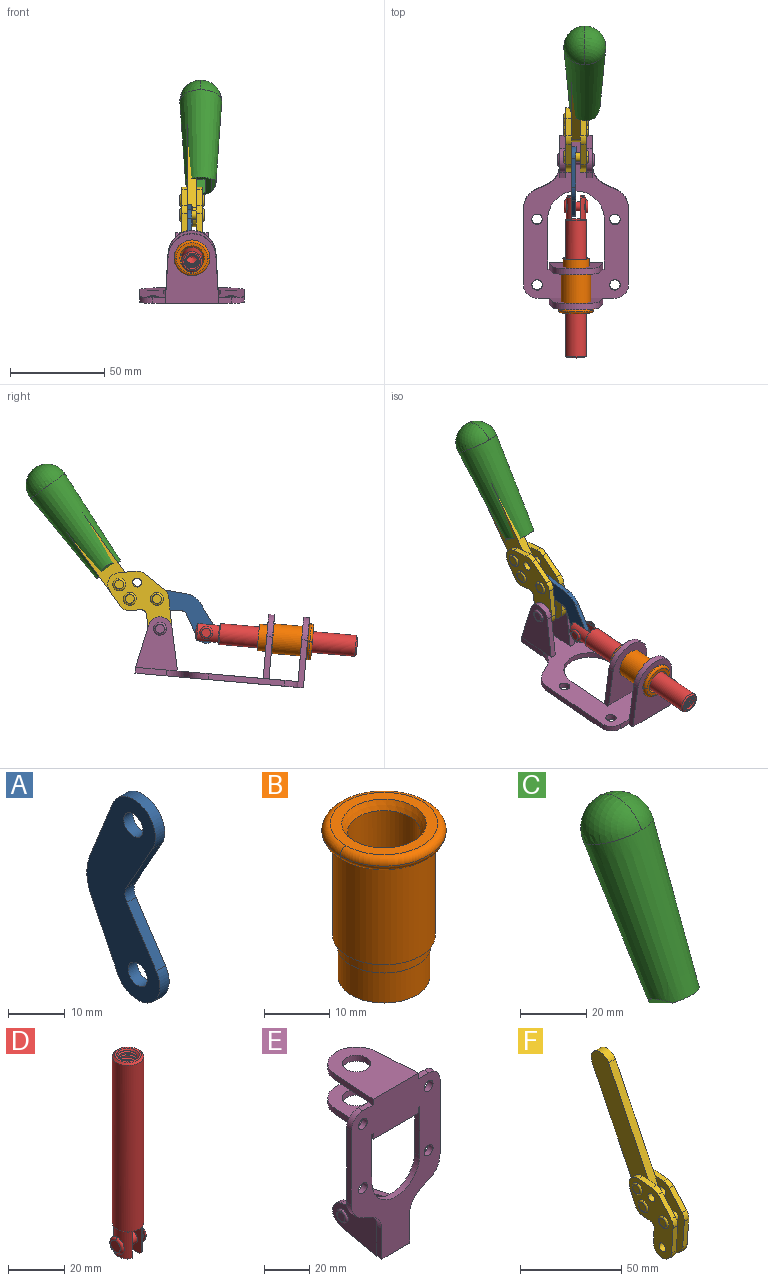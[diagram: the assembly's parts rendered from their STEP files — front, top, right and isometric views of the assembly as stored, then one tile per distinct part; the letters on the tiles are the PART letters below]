
ASSEMBLY  parts=6 mates=6
PART A: 12 faces, bbox 2.3x18.2x42.8 mm
  f0: cylinder r=2.4mm len=4.8mm, axis (1,0,0), area 34.9mm2, adj f4,f11
  f1: cylinder r=10.41mm len=8.47mm, axis (1,0,0), area 20.2mm2, adj f4,f9,f10,f11
  f2: cylinder r=3.05mm len=3.16mm, axis (1,0,0), area 7.7mm2, adj f4,f6,f7,f11
  f3: cylinder r=2.4mm len=4.8mm, axis (1,0,0), area 34.9mm2, adj f4,f11
  f4: plane 42.81x18.23mm, normal (-1,0,0), area 414.1mm2, adj f0,f1,f2,f3,f5,f6,f7,f8
  f5: cylinder r=5.54mm len=10.67mm, axis (1,0,0), area 41.8mm2, adj f4,f6,f10,f11
  f6: plane 11.66x6.53mm, normal (0,-0.87,-0.49), area 30.9mm2, adj f2,f4,f5,f11
  f7: plane 11.17x7.33mm, normal (0,-0.84,0.55), area 30.9mm2, adj f2,f4,f8,f11
  f8: cylinder r=5.54mm len=10.51mm, axis (1,0,0), area 41.8mm2, adj f4,f7,f9,f11
  f9: plane 13.67x6.67mm, normal (0,0.9,-0.44), area 35.1mm2, adj f1,f4,f8,f11
  f10: plane 14.1x5.7mm, normal (0,0.93,0.37), area 35.1mm2, adj f1,f4,f5,f11
  f11: plane 42.81x18.23mm, normal (1,0,0), area 414.1mm2, adj f0,f1,f2,f3,f5,f6,f7,f8
PART B: 15 faces, bbox 20.6x20.6x28.7 mm
  f0: torus R=8.26mm, axis (0,0,1), area 56.8mm2, adj f1,f10,f12
  f1: torus R=8.26mm, axis (0,0,1), area 56.8mm2, adj f0,f6,f13
  f2: cylinder r=5.59mm len=25.91mm, axis (0,0,1), area 909.6mm2, adj f3,f4
  f3: cone r=6.86mm half-angle=45deg, axis (0,0,-1), area 70.2mm2, adj f2,f14
  f4: cone r=6.47mm half-angle=30deg, axis (0,0,1), area 66.7mm2, adj f2,f13
  f5: cylinder r=7.04mm len=14.07mm, axis (0,0,1), area 252.6mm2, adj f11,f14
  f6: torus R=8.26mm, axis (0,0,1), area 56.8mm2, adj f1,f12,f13
  f7: cylinder r=7.16mm len=14.33mm, axis (0,0,1), area 91.5mm2, adj f9,f11
  f8: cylinder r=7.86mm len=18.42mm, axis (0,0,1), area 909.6mm2, adj f9,f10
  f9: plane 15.72x15.72mm, normal (0,0,-1), area 33mm2, adj f7,f8
  f10: plane 16.51x16.51mm, normal (0,0,-1), area 19.9mm2, adj f0,f8,f12
  f11: plane 14.33x14.33mm, normal (0,0,-1), area 5.7mm2, adj f5,f7
  f12: torus R=8.26mm, axis (0,0,1), area 56.8mm2, adj f0,f6,f10
  f13: plane 16.51x16.51mm, normal (0,0,1), area 82.7mm2, adj f1,f4,f6
  f14: plane 14.07x14.07mm, normal (0,0,-1), area 7.8mm2, adj f3,f5
PART C: 11 faces, bbox 22.3x42.6x64.5 mm
  f0: sphere r=11.13mm, area 411.4mm2, adj f1,f8
  f1: cone r=11.11mm half-angle=3.3deg, axis (0,0.44,0.9), area 3251.8mm2, adj f0,f7,f8,f9,f10
  f2: cylinder r=6.16mm len=11.7mm, axis (1,0,0), area 89.5mm2, adj f3,f4,f5,f6
  f3: plane 60.23x36.75mm, normal (-1,0,0), area 763.6mm2, adj f2,f4,f6,f10
  f4: plane 51.37x25.05mm, normal (0,0.9,-0.44), area 264.2mm2, adj f2,f3,f5,f10
  f5: plane 60.23x36.75mm, normal (1,0,0), area 763.6mm2, adj f2,f4,f6,f10
  f6: plane 51.37x25.05mm, normal (0,-0.9,0.44), area 264.2mm2, adj f2,f3,f5,f10
  f7: plane 9.95x5.95mm, normal (0.71,-0.31,-0.64), area 25.8mm2, adj f1,f10
  f8: sphere r=11.13mm, area 411.4mm2, adj f0,f1
  f9: plane 9.95x5.95mm, normal (-0.71,-0.31,-0.64), area 25.8mm2, adj f1,f10
  f10: plane 14.27x11.38mm, normal (0,-0.44,-0.9), area 106.7mm2, adj f1,f3,f4,f5,f6,f7,f9
PART D: 48 faces, bbox 12.6x11.1x86.1 mm
  f0: torus R=2.41mm, axis (-1,0,0), area 15mm2, adj f30,f32,f34
  f1: torus R=2.41mm, axis (-1,0,0), area 15mm2, adj f29,f31,f33
  f2: cylinder r=5.54mm len=72.39mm, axis (0,0,1), area 2518.5mm2, adj f3,f4,f42,f43
  f3: cone r=5.54mm half-angle=45deg, axis (0,0,1), area 7.6mm2, adj f2,f5,f41
  f4: cone r=5.54mm half-angle=45deg, axis (0,0,-1), area 34.9mm2, adj f2,f39
  f5: cylinder r=5.08mm len=11.48mm, axis (0,0,1), area 108.3mm2, adj f3,f7,f8,f41
  f6: cylinder r=2.41mm len=4.83mm, axis (-1,0,0), area 71.2mm2, adj f40,f41
  f7: cylinder r=2.41mm len=4.83mm, axis (-1,0,0), area 7.6mm2, adj f5,f34
  f8: cone r=5.08mm half-angle=45deg, axis (0,0,1), area 10.6mm2, adj f5,f37,f41
  f9: cone r=3.98mm half-angle=45deg, axis (0,0,1), area 17.6mm2, adj f27,f39,f45,f46,f47
  f10: cylinder r=2.41mm len=4.83mm, axis (-1,0,0), area 7.6mm2, adj f33,f38
  f11: cylinder r=3.2mm len=6.4mm, axis (0,0,1), area 78.4mm2, adj f12,f28,f44,f45,f47
  f12: cylinder r=3.2mm len=6.4mm, axis (0,0,1), area 10.5mm2, adj f11,f13,f45,f47
  f13: cylinder r=3.2mm len=6.4mm, axis (0,0,1), area 10.5mm2, adj f12,f14,f45,f47
  f14: cylinder r=3.2mm len=6.4mm, axis (0,0,1), area 10.5mm2, adj f13,f15,f45,f47
  f15: cylinder r=3.2mm len=6.4mm, axis (0,0,1), area 10.5mm2, adj f14,f16,f45,f47
  f16: cylinder r=3.2mm len=6.4mm, axis (0,0,1), area 10.5mm2, adj f15,f17,f45,f47
  f17: cylinder r=3.2mm len=6.4mm, axis (0,0,1), area 10.5mm2, adj f16,f18,f45,f47
  f18: cylinder r=3.2mm len=6.4mm, axis (0,0,1), area 10.5mm2, adj f17,f19,f45,f47
  f19: cylinder r=3.2mm len=6.4mm, axis (0,0,1), area 10.5mm2, adj f18,f20,f45,f47
  f20: cylinder r=3.2mm len=6.4mm, axis (0,0,1), area 10.5mm2, adj f19,f21,f45,f47
  f21: cylinder r=3.2mm len=6.4mm, axis (0,0,1), area 10.5mm2, adj f20,f22,f45,f47
  f22: cylinder r=3.2mm len=6.4mm, axis (0,0,1), area 10.5mm2, adj f21,f23,f45,f47
  f23: cylinder r=3.2mm len=6.4mm, axis (0,0,1), area 10.5mm2, adj f22,f24,f45,f47
  f24: cylinder r=3.2mm len=6.4mm, axis (0,0,1), area 10.5mm2, adj f23,f25,f45,f47
  f25: cylinder r=3.2mm len=6.4mm, axis (0,0,1), area 10.5mm2, adj f24,f26,f45,f47
  f26: cylinder r=3.2mm len=6.4mm, axis (0,0,1), area 10.5mm2, adj f25,f27,f45,f47
  f27: cylinder r=3.2mm len=6.4mm, axis (0,0,1), area 7.4mm2, adj f9,f26,f45,f47
  f28: cone r=3.2mm half-angle=60deg, axis (0,0,1), area 37.2mm2, adj f11
  f29: plane 4.83x4.83mm, normal (-1,0,0), area 18.3mm2, adj f1,f31
  f30: plane 4.83x4.83mm, normal (1,0,0), area 18.3mm2, adj f0,f32
  f31: torus R=2.41mm, axis (-1,0,0), area 15mm2, adj f1,f29,f33
  f32: torus R=2.41mm, axis (-1,0,0), area 15mm2, adj f0,f30,f34
  f33: plane 6.83x6.83mm, normal (1,0,0), area 18.3mm2, adj f1,f10,f31
  f34: plane 6.83x6.83mm, normal (-1,0,0), area 18.3mm2, adj f0,f7,f32
  f35: cone r=5.08mm half-angle=45deg, axis (0,0,1), area 10.6mm2, adj f36,f38,f40
  f36: plane 7.25x1.97mm, normal (0,0,-1), area 10mm2, adj f35,f40
  f37: plane 7.25x1.97mm, normal (0,0,-1), area 10mm2, adj f8,f41
  f38: cylinder r=5.08mm len=11.48mm, axis (0,0,1), area 108.3mm2, adj f10,f35,f40,f42
  f39: plane 9.55x9.55mm, normal (0,0,1), area 22mm2, adj f4,f9
  f40: plane 12.76x10.09mm, normal (1,0,0), area 95.7mm2, adj f6,f35,f36,f38,f42,f43
  f41: plane 12.76x10.09mm, normal (-1,0,0), area 95.7mm2, adj f3,f5,f6,f8,f37,f43
  f42: cone r=5.54mm half-angle=45deg, axis (0,0,1), area 7.6mm2, adj f2,f38,f40
  f43: plane 11.07x4.7mm, normal (0,0,-1), area 50.4mm2, adj f2,f40,f41
  f44: plane 0.89x0.62mm, normal (-1,0,0), area 0.3mm2, adj f11,f45,f46,f47
  f45: bspline ~24.8x7.63mm, area 266.6mm2, adj f9,f11,f12,f13,f14,f15,f16,f17
  f46: bspline ~24.87x7.63mm, area 73.6mm2, adj f9,f44,f45,f47
  f47: bspline ~24.98x7.63mm, area 272.5mm2, adj f9,f11,f12,f13,f14,f15,f16,f17
PART E: 55 faces, bbox 55.7x37.4x89.8 mm
  f0: torus R=2.41mm, axis (-1,0,0), area 15mm2, adj f11,f15,f25
  f1: torus R=2.41mm, axis (-1,0,0), area 15mm2, adj f10,f12,f22
  f2: cylinder r=2.78mm len=5.56mm, axis (0,-1,0), area 54.2mm2, adj f30,f54
  f3: cylinder r=14.99mm len=29.97mm, axis (0,-1,0), area 145.9mm2, adj f30,f49,f53,f54
  f4: cylinder r=2.78mm len=5.56mm, axis (0,-1,0), area 54.2mm2, adj f30,f54
  f5: cylinder r=2.78mm len=5.56mm, axis (0,-1,0), area 54.2mm2, adj f30,f54
  f6: cylinder r=2.78mm len=5.56mm, axis (0,-1,0), area 54.2mm2, adj f30,f54
  f7: cylinder r=6.35mm len=12.7mm, axis (0,0,1), area 123.6mm2, adj f27,f51
  f8: cylinder r=6.35mm len=12.7mm, axis (0,0,-1), area 124.7mm2, adj f21,f35
  f9: cylinder r=2.41mm len=11.18mm, axis (-1,0,0), area 169.4mm2, adj f16,f19
  f10: plane 4.83x4.83mm, normal (1,0,0), area 18.3mm2, adj f1,f12
  f11: plane 4.83x4.83mm, normal (-1,0,0), area 18.3mm2, adj f0,f15
  f12: torus R=2.41mm, axis (-1,0,0), area 15mm2, adj f1,f10,f22
  f13: cylinder r=6.35mm len=12.41mm, axis (1,0,0), area 53.4mm2, adj f18,f19,f22,f23
  f14: cylinder r=6.35mm len=12.41mm, axis (-1,0,0), area 53.4mm2, adj f16,f17,f24,f25
  f15: torus R=2.41mm, axis (-1,0,0), area 15mm2, adj f0,f11,f25
  f16: plane 27.86x22.35mm, normal (1,0,0), area 425.4mm2, adj f9,f14,f17,f24,f30
  f17: plane 22.86x4.97mm, normal (0,0.21,0.98), area 72.5mm2, adj f14,f16,f25,f30
  f18: plane 22.86x4.97mm, normal (0,0.21,0.98), area 72.5mm2, adj f13,f19,f22,f30
  f19: plane 27.86x22.35mm, normal (-1,0,0), area 425.4mm2, adj f9,f13,f18,f23,f30
  f20: cylinder r=12.7mm len=25.35mm, axis (0,0,-1), area 119.8mm2, adj f21,f34,f35,f36
  f21: plane 34.21x28.07mm, normal (0,0,-1), area 702.4mm2, adj f8,f20,f30,f34,f36
  f22: plane 27.96x22.45mm, normal (1,0,0), area 407.2mm2, adj f1,f12,f13,f18,f23,f30,f42,f43
  f23: plane 22.86x4.97mm, normal (0,0.21,-0.98), area 72.5mm2, adj f13,f19,f22,f44
  f24: plane 22.86x4.97mm, normal (0,0.21,-0.98), area 72.5mm2, adj f14,f16,f25,f44
  f25: plane 27.86x22.35mm, normal (-1,0,0), area 407.1mm2, adj f0,f14,f15,f17,f24,f30,f45,f46
  f26: plane 3.1x0.95mm, normal (0,0,-1), area 2.7mm2, adj f30,f49,f50,f54
  f27: plane 34.21x28.07mm, normal (0,0,1), area 702.4mm2, adj f7,f28,f30,f50,f52
  f28: cylinder r=12.7mm len=25.35mm, axis (0,0,1), area 118.8mm2, adj f27,f50,f51,f52
  f29: plane 3.1x0.95mm, normal (0,0,-1), area 2.7mm2, adj f30,f52,f53,f54
  f30: plane 86.54x55.63mm, normal (0,1,0), area 2362.9mm2, adj f2,f3,f4,f5,f6,f16,f17,f18
  f31: plane 40.56x3.1mm, normal (-1,0,0), area 125.7mm2, adj f30,f32,f48,f54
  f32: cylinder r=7.11mm len=7.11mm, axis (0,-1,0), area 34.6mm2, adj f30,f31,f33,f54
  f33: plane 6.67x3.1mm, normal (0,0,1), area 20.4mm2, adj f30,f32,f34,f54
  f34: plane 25.39x3.13mm, normal (-1,0.06,0), area 79.5mm2, adj f20,f21,f33,f35,f54
  f35: plane 37.31x28.45mm, normal (0,0,1), area 789.9mm2, adj f8,f20,f34,f36,f54
  f36: plane 25.39x3.13mm, normal (1,0.06,0), area 79.5mm2, adj f20,f21,f35,f37,f54
  f37: plane 6.67x3.1mm, normal (0,0,1), area 20.4mm2, adj f30,f36,f38,f54
  f38: cylinder r=7.11mm len=7.11mm, axis (0,-1,0), area 34.6mm2, adj f30,f37,f39,f54
  f39: plane 40.56x3.1mm, normal (1,0,0), area 125.7mm2, adj f30,f38,f40,f54
  f40: cylinder r=11.18mm len=10.16mm, axis (0,-1,0), area 39.5mm2, adj f30,f39,f41,f54
  f41: plane 6.09x3.1mm, normal (0.42,0,-0.91), area 20.8mm2, adj f30,f40,f42,f54
  f42: cylinder r=11.18mm len=9.41mm, axis (0,-1,0), area 37.2mm2, adj f22,f30,f41,f43,f54
  f43: plane 16.5x3.1mm, normal (1,0,0), area 51.1mm2, adj f22,f42,f44,f54
  f44: plane 17.37x3.1mm, normal (0,0,-1), area 53.8mm2, adj f23,f24,f30,f43,f45,f54
  f45: plane 16.5x3.1mm, normal (-1,0,0), area 51.1mm2, adj f25,f44,f46,f54
  f46: cylinder r=11.18mm len=9.41mm, axis (0,-1,0), area 37.2mm2, adj f25,f30,f45,f47,f54
  f47: plane 6.09x3.1mm, normal (-0.42,0,-0.91), area 20.8mm2, adj f30,f46,f48,f54
  f48: cylinder r=11.18mm len=10.16mm, axis (0,-1,0), area 39.5mm2, adj f30,f31,f47,f54
  f49: plane 26.54x3.1mm, normal (-1,0,0), area 82.3mm2, adj f3,f26,f30,f54
  f50: plane 25.39x3.1mm, normal (1,0.06,0), area 78.8mm2, adj f26,f27,f28,f51,f54
  f51: plane 37.31x28.45mm, normal (0,0,-1), area 789.9mm2, adj f7,f28,f50,f52,f54
  f52: plane 25.39x3.1mm, normal (-1,0.06,0), area 78.8mm2, adj f27,f28,f29,f51,f54
  f53: plane 26.54x3.1mm, normal (1,0,0), area 82.3mm2, adj f3,f29,f30,f54
  f54: plane 89.66x55.63mm, normal (0,-1,0), area 2678.5mm2, adj f2,f3,f4,f5,f6,f26,f29,f31
PART F: 59 faces, bbox 12.9x60.2x99.6 mm
  f0: torus R=2.39mm, axis (-1,0,0), area 14.9mm2, adj f20,f43,f51
  f1: torus R=2.39mm, axis (-1,0,0), area 14.9mm2, adj f19,f42,f51
  f2: torus R=2.39mm, axis (-1,0,0), area 14.9mm2, adj f18,f35,f51
  f3: torus R=2.39mm, axis (-1,0,0), area 14.9mm2, adj f14,f17,f23
  f4: torus R=2.39mm, axis (-1,0,0), area 14.9mm2, adj f13,f16,f23
  f5: torus R=2.39mm, axis (-1,0,0), area 14.9mm2, adj f12,f15,f23
  f6: cylinder r=2.39mm len=4.78mm, axis (1,0,0), area 46.5mm2, adj f48,f50,f51
  f7: cylinder r=2.39mm len=4.78mm, axis (1,0,0), area 46.5mm2, adj f50,f51
  f8: cylinder r=6.35mm len=12.68mm, axis (1,0,0), area 61.8mm2, adj f38,f39,f50,f51
  f9: cylinder r=2.39mm len=4.78mm, axis (-1,0,0), area 70.5mm2, adj f46,f50
  f10: cylinder r=2.39mm len=4.78mm, axis (-1,0,0), area 46.5mm2, adj f23,f45,f46
  f11: cylinder r=2.39mm len=4.78mm, axis (-1,0,0), area 46.5mm2, adj f23,f46
  f12: plane 4.78x4.78mm, normal (1,0,0), area 17.9mm2, adj f5,f15
  f13: plane 4.78x4.78mm, normal (1,0,0), area 17.9mm2, adj f4,f16
  f14: plane 4.78x4.78mm, normal (1,0,0), area 17.9mm2, adj f3,f17
  f15: torus R=2.39mm, axis (-1,0,0), area 14.9mm2, adj f5,f12,f23
  f16: torus R=2.39mm, axis (-1,0,0), area 14.9mm2, adj f4,f13,f23
  f17: torus R=2.39mm, axis (-1,0,0), area 14.9mm2, adj f3,f14,f23
  f18: plane 4.78x4.78mm, normal (-1,0,0), area 17.9mm2, adj f2,f35
  f19: plane 4.78x4.78mm, normal (-1,0,0), area 17.9mm2, adj f1,f42
  f20: plane 4.78x4.78mm, normal (-1,0,0), area 17.9mm2, adj f0,f43
  f21: plane 2.26x0.2mm, normal (1,0,0), area 0.2mm2, adj f31,f44
  f22: plane 2.26x0.2mm, normal (-1,0,0), area 0.2mm2, adj f41,f44
  f23: plane 39.37x30.77mm, normal (1,0,0), area 565.5mm2, adj f3,f4,f5,f10,f11,f15,f16,f17
  f24: cylinder r=6.1mm len=4.15mm, axis (-1,0,0), area 14.7mm2, adj f23,f25,f32,f46
  f25: plane 10.25x9.01mm, normal (0,-0.75,0.66), area 42.3mm2, adj f23,f24,f26,f46
  f26: cylinder r=6.35mm len=4.64mm, axis (-1,0,0), area 15.6mm2, adj f23,f25,f27,f46
  f27: plane 15.84x3.1mm, normal (0,-1,-0.07), area 49.2mm2, adj f23,f26,f28,f46
  f28: cylinder r=6.35mm len=12.68mm, axis (-1,0,0), area 61.8mm2, adj f23,f27,f29,f46
  f29: plane 8.11x3.1mm, normal (0,1,0.07), area 25.2mm2, adj f23,f28,f30,f46
  f30: cylinder r=3.05mm len=3.25mm, axis (-1,0,0), area 14.8mm2, adj f23,f29,f31,f46
  f31: plane 5.99x3.1mm, normal (0,0.07,-1), area 18.6mm2, adj f21,f23,f30,f44,f46
  f32: plane 9.5x3.1mm, normal (0,-0.07,1), area 29.5mm2, adj f23,f24,f33,f46,f47
  f33: cylinder r=6.1mm len=8.63mm, axis (-1,0,0), area 39.1mm2, adj f23,f32,f34,f47
  f34: plane 8.65x3.96mm, normal (0,0.91,-0.42), area 29.5mm2, adj f23,f33,f44,f47
  f35: torus R=2.39mm, axis (-1,0,0), area 14.9mm2, adj f2,f18,f51
  f36: plane 10.25x9.01mm, normal (0,-0.75,0.66), area 42.3mm2, adj f37,f49,f50,f51
  f37: cylinder r=6.35mm len=4.64mm, axis (1,0,0), area 15.6mm2, adj f36,f38,f50,f51
  f38: plane 15.84x3.1mm, normal (0,-1,-0.07), area 49.2mm2, adj f8,f37,f50,f51
  f39: plane 8.11x3.1mm, normal (0,1,0.07), area 25.2mm2, adj f8,f40,f50,f51
  f40: cylinder r=3.05mm len=3.25mm, axis (1,0,0), area 14.8mm2, adj f39,f41,f50,f51
  f41: plane 5.99x3.1mm, normal (0,0.07,-1), area 18.6mm2, adj f22,f40,f44,f50,f51
  f42: torus R=2.39mm, axis (-1,0,0), area 14.9mm2, adj f1,f19,f51
  f43: torus R=2.39mm, axis (-1,0,0), area 14.9mm2, adj f0,f20,f51
  f44: cylinder r=6.35mm len=12.12mm, axis (-1,0,0), area 128.9mm2, adj f21,f22,f23,f31,f34,f41,f46,f47
  f45: plane 2.65x1.35mm, normal (1,0,0), area 1mm2, adj f10,f55
  f46: plane 39.08x20.42mm, normal (-1,0,0), area 412.5mm2, adj f9,f10,f11,f24,f25,f26,f27,f28
  f47: plane 77.62x39.82mm, normal (1,0,0), area 850mm2, adj f32,f33,f34,f44,f53,f54,f55
  f48: plane 2.65x1.35mm, normal (-1,0,0), area 1mm2, adj f6,f55
  f49: cylinder r=6.1mm len=4.15mm, axis (1,0,0), area 14.7mm2, adj f36,f50,f51,f56
  f50: plane 39.08x20.42mm, normal (1,0,0), area 412.5mm2, adj f6,f7,f8,f9,f36,f37,f38,f39
  f51: plane 39.37x30.77mm, normal (-1,0,0), area 565.5mm2, adj f0,f1,f2,f6,f7,f8,f35,f36
  f52: plane 8.65x3.96mm, normal (0,0.91,-0.42), area 29.5mm2, adj f44,f51,f57,f58
  f53: plane 68.49x33.4mm, normal (0,0.9,-0.44), area 358.1mm2, adj f44,f47,f54,f58
  f54: cylinder r=6.35mm len=12.06mm, axis (1,0,0), area 93.7mm2, adj f47,f53,f55,f58
  f55: plane 68.49x33.4mm, normal (0,-0.9,0.44), area 358.1mm2, adj f44,f45,f46,f47,f48,f50,f54,f58
  f56: plane 9.5x3.1mm, normal (0,-0.07,1), area 29.5mm2, adj f49,f50,f51,f57,f58
  f57: cylinder r=6.1mm len=8.63mm, axis (1,0,0), area 39.1mm2, adj f51,f52,f56,f58
  f58: plane 77.62x39.82mm, normal (-1,0,0), area 850mm2, adj f44,f52,f53,f54,f55,f56,f57
PLACE A rot(axis=(1,0,0),126.4deg) t=(-28.7,86.21,-25.62)mm
PLACE B rot(axis=(1,0,0),95deg) t=(-27.54,53.87,-40.15)mm
PLACE C rot(axis=(-1,0,0),10deg) t=(-22.88,65.03,23.04)mm
PLACE D rot(axis=(1,0,0),95deg) t=(-27.54,76.71,-38.16)mm
PLACE E rot(axis=(1,0,0),95deg) t=(-27.54,53.87,-40.15)mm fixed
PLACE F rot(axis=(-1,0,0),10deg) t=(-27.54,65.03,23.04)mm
MATE fastened B.f2 <-> E.f7  axis (0,1,0.09) through (-27.54,5.51,-19.68)mm
MATE revolute A.f3 <-> F.f4  axis (-1,0,0) through (-27.54,85.35,2.95)mm
MATE fastened C.f2 <-> F.f54  axis (1,0,0) through (-25.19,144.5,64.65)mm
MATE slider E.f7 <-> D.f2  axis (0,-1,-0.09) through (-27.54,5.51,-19.68)mm
MATE revolute E.f0 <-> F.f7  axis (-1,0,0) through (-27.54,83.69,-12.84)mm
MATE revolute A.f5 <-> D.f6  axis (-1,0,0) through (-27.54,59.15,-14.99)mm
